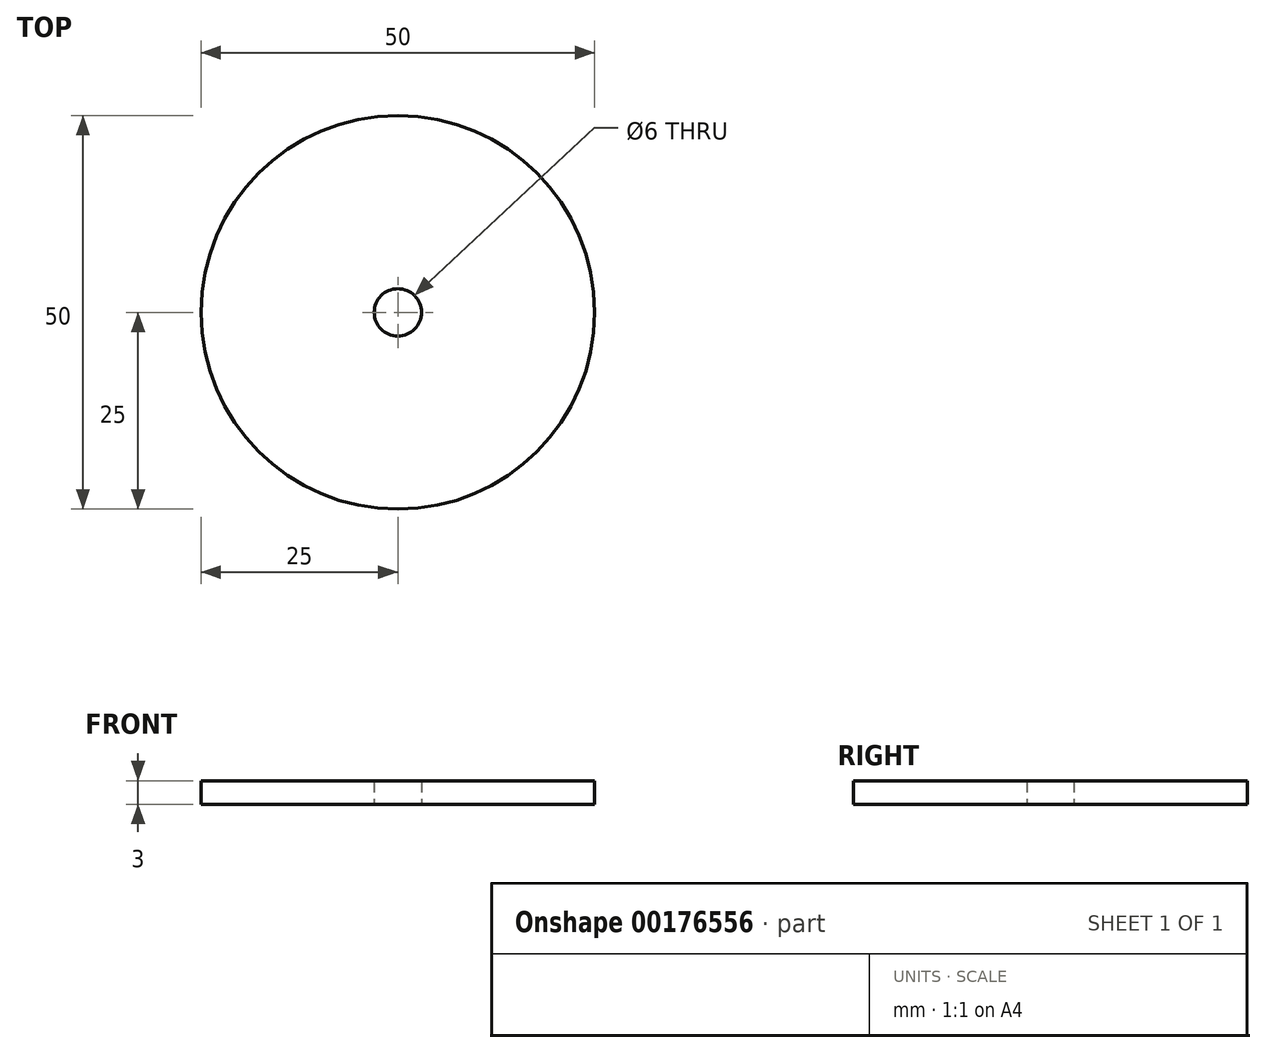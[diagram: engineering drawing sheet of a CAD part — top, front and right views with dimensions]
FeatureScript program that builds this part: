
annotation { "Feature Type Name" : "Feature", "Feature Type Description" : "" }
export const myFeature = defineFeature(function(context is Context, id is Id, definition is map)
    precondition{}
    {
        {
            var Q0;
            Q0=qCreatedBy(makeId("Top.planeOp"),FACE);
            var sketch = newSketch(context, id + "F0", { "sketchPlane" : qUnion([Q0])});
            skLineSegment(sketch, "E0", {"start": v(0, 25) * mm, "end": v(0, -25) * mm});
            skCircle(sketch, "E1", {"center": v(0, 0) * mm, "radius": 25 * mm});
            skCircle(sketch, "E2", {"center": v(0, 0) * mm, "radius": 3 * mm});
            skSolve(sketch);
        }
        {
            var Q0;
            Q0 = qSketchRegion(id + "F0", true);
            extrude(context, id + "F1", {"entities" : qUnion([Q0]), "depth" : 3 * mm});
        }
    });
